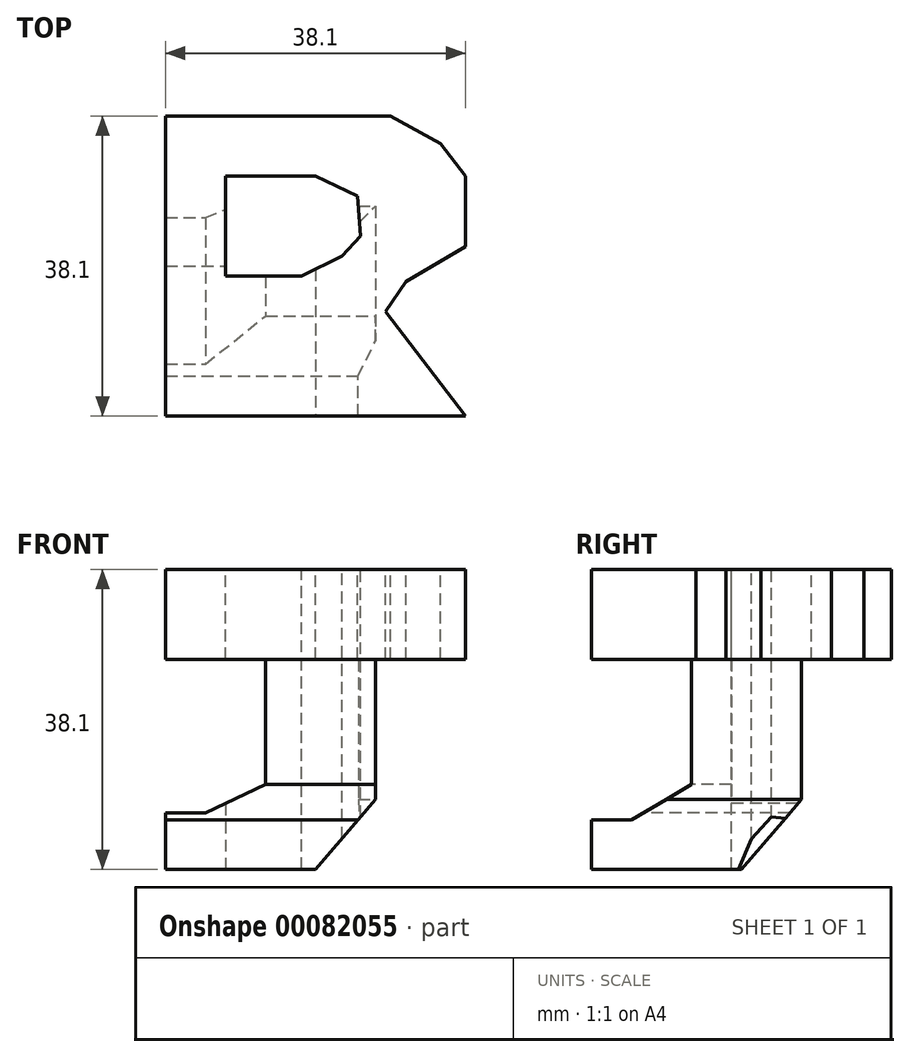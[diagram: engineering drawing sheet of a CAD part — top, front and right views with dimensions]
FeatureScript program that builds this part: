
annotation { "Feature Type Name" : "Feature", "Feature Type Description" : "" }
export const myFeature = defineFeature(function(context is Context, id is Id, definition is map)
    precondition{}
    {
        {
            var Q0;
            Q0=qCreatedBy(makeId("Top.planeOp"),FACE);
            cPlane(context, id + "F0", {"entities" : qUnion([Q0]), "cplaneType" : CPlaneType.OFFSET, "offset" : 38.1 * mm, "width" : 152.4 * mm, "height" : 152.4 * mm});
        }
        {
            var Q0;
            Q0=qCreatedBy(makeId("Front.planeOp"),FACE);
            cPlane(context, id + "F1", {"entities" : qUnion([Q0]), "cplaneType" : CPlaneType.OFFSET, "offset" : 38.1 * mm, "width" : 152.4 * mm, "height" : 152.4 * mm});
        }
        {
            var Q0;
            Q0=qCreatedBy(makeId("Right.planeOp"),FACE);
            cPlane(context, id + "F2", {"entities" : qUnion([Q0]), "cplaneType" : CPlaneType.OFFSET, "offset" : 38.1 * mm, "width" : 152.4 * mm, "height" : 152.4 * mm});
        }
        {
            var Q0;
            Q0=qCreatedBy(makeId("Front.planeOp"),FACE);
            var sketch = newSketch(context, id + "F3", { "sketchPlane" : qUnion([Q0])});
            skLineSegment(sketch, "E0", {"start": v(0, 0) * mm, "end": v(0, 38.1) * mm});
            skLineSegment(sketch, "E1", {"start": v(0, 38.1) * mm, "end": v(38.1, 38.1) * mm});
            skLineSegment(sketch, "E2", {"start": v(38.1, 38.1) * mm, "end": v(38.1, 0) * mm});
            skLineSegment(sketch, "E3", {"start": v(38.1, 0) * mm, "end": v(0, 0) * mm});
            skSolve(sketch);
        }
        {
            var Q0;
            Q0 = qSketchRegion(id + "F3", true);
            extrude(context, id + "F4", {"entities" : qUnion([Q0]), "depth" : 38.1 * mm});
        }
        {
            var Q0;
            Q0=qCreatedBy(id+"F1.planeOp",FACE);
            var sketch = newSketch(context, id + "F5", { "sketchPlane" : qUnion([Q0])});
            skLineSegment(sketch, "E4", {"start": v(0, 0) * mm, "end": v(0, 38.1) * mm});
            skLineSegment(sketch, "E5", {"start": v(0, 38.1) * mm, "end": v(38.1, 38.1) * mm});
            skLineSegment(sketch, "E6", {"start": v(38.1, 38.1) * mm, "end": v(38.1, 0) * mm});
            skLineSegment(sketch, "E7", {"start": v(38.1, 0) * mm, "end": v(0, 0) * mm});
            skLineSegment(sketch, "E8", {"start": v(0, 26.67) * mm, "end": v(12.7, 26.67) * mm});
            skLineSegment(sketch, "E9", {"start": v(38.1, 26.67) * mm, "end": v(26.67, 26.67) * mm});
            skPoint(sketch, "E10.end.orphan", {"position": v(19.05, 0) * mm});
            skLineSegment(sketch, "E11", {"start": v(26.67, 26.67) * mm, "end": v(26.67, 8.89) * mm});
            skLineSegment(sketch, "E12", {"start": v(26.67, 8.89) * mm, "end": v(19.05, 0) * mm});
            skLineSegment(sketch, "E13", {"start": v(12.7, 26.67) * mm, "end": v(12.7, 10.8) * mm});
            skLineSegment(sketch, "E14", {"start": v(12.7, 10.8) * mm, "end": v(5.08, 7.17) * mm});
            skLineSegment(sketch, "E15", {"start": v(5.08, 7.17) * mm, "end": v(0, 7.17) * mm});
            skSolve(sketch);
        }
        {
            var Q0;
            {var subQ0=sQuery(id+"F5.wireOp",EDGE,"E8");Q0=makeQuery(id+"F5.imprint","IMPRINT",FACE,{"disambiguationData":[TD([[makeQuery(id+"F5.imprint","IMPRINT",EDGE,{"derivedFrom":subQ0}),-1.0]])]});}
            var Q1;
            {var subQ0=sQuery(id+"F5.wireOp",EDGE,"E9");Q1=makeQuery(id+"F5.imprint","IMPRINT",FACE,{"disambiguationData":[TD([[makeQuery(id+"F5.imprint","IMPRINT",EDGE,{"derivedFrom":subQ0}),1.0]])]});}
            extrude(context, id + "F6", {"entities" : qUnion([Q0, Q1]), "operationType" : NewBodyOperationType.REMOVE, "oppositeDirection" : true, "depth" : 38.1 * mm});
        }
        {
            var Q0;
            Q0=qCreatedBy(id+"F2.planeOp",FACE);
            var sketch = newSketch(context, id + "F7", { "sketchPlane" : qUnion([Q0])});
            skLineSegment(sketch, "E16", {"start": v(0, 0) * mm, "end": v(0, 38.1) * mm});
            skLineSegment(sketch, "E17", {"start": v(0, 38.1) * mm, "end": v(-38.1, 38.1) * mm});
            skLineSegment(sketch, "E18", {"start": v(-38.1, 38.1) * mm, "end": v(-38.1, 0) * mm});
            skLineSegment(sketch, "E19", {"start": v(-38.1, 0) * mm, "end": v(0, 0) * mm});
            skLineSegment(sketch, "E20", {"start": v(-38.1, 26.67) * mm, "end": v(-25.4, 26.67) * mm});
            skLineSegment(sketch, "E21", {"start": v(-25.4, 26.67) * mm, "end": v(-25.4, 10.8) * mm});
            skLineSegment(sketch, "E22", {"start": v(-25.4, 10.8) * mm, "end": v(-33.02, 6.27) * mm});
            skLineSegment(sketch, "E23", {"start": v(-33.02, 6.27) * mm, "end": v(-38.1, 6.27) * mm});
            skLineSegment(sketch, "E24", {"start": v(0, 26.67) * mm, "end": v(-11.43, 26.67) * mm});
            skLineSegment(sketch, "E25", {"start": v(-11.43, 26.67) * mm, "end": v(-11.43, 8.89) * mm});
            skLineSegment(sketch, "E26", {"start": v(-11.43, 8.89) * mm, "end": v(-19.05, 0) * mm});
            skSolve(sketch);
        }
        {
            var Q0;
            {var subQ0=sQuery(id+"F7.wireOp",EDGE,"E20");Q0=makeQuery(id+"F7.imprint","IMPRINT",FACE,{"disambiguationData":[TD([[makeQuery(id+"F7.imprint","IMPRINT",EDGE,{"derivedFrom":subQ0}),-1.0]])]});}
            var Q1;
            {var subQ0=sQuery(id+"F7.wireOp",EDGE,"E24");Q1=makeQuery(id+"F7.imprint","IMPRINT",FACE,{"disambiguationData":[TD([[makeQuery(id+"F7.imprint","IMPRINT",EDGE,{"derivedFrom":subQ0}),1.0]])]});}
            extrude(context, id + "F8", {"entities" : qUnion([Q0, Q1]), "operationType" : NewBodyOperationType.REMOVE, "oppositeDirection" : true, "depth" : 38.1 * mm});
        }
        {
            var Q0;
            Q0=qCreatedBy(id+"F0.planeOp",FACE);
            var sketch = newSketch(context, id + "F9", { "sketchPlane" : qUnion([Q0])});
            skLineSegment(sketch, "E27", {"start": v(0, 0) * mm, "end": v(38.1, 0) * mm});
            skLineSegment(sketch, "E28", {"start": v(38.1, 0) * mm, "end": v(38.1, -38.1) * mm});
            skLineSegment(sketch, "E29", {"start": v(38.1, -38.1) * mm, "end": v(0, -38.1) * mm});
            skLineSegment(sketch, "E30", {"start": v(0, -38.1) * mm, "end": v(0, 0) * mm});
            skLineSegment(sketch, "E31", {"start": v(7.62, -7.62) * mm, "end": v(19.05, -7.62) * mm});
            skLineSegment(sketch, "E32", {"start": v(19.05, -7.62) * mm, "end": v(24.4, -10.16) * mm});
            skLineSegment(sketch, "E33", {"start": v(24.4, -10.16) * mm, "end": v(24.75, -15.24) * mm});
            skLineSegment(sketch, "E34", {"start": v(24.75, -15.24) * mm, "end": v(22.4, -17.78) * mm});
            skPoint(sketch, "E35.orphan", {"position": v(38.1, -7.62) * mm});
            skPoint(sketch, "E36.end.orphan", {"position": v(0, -21.23) * mm});
            skLineSegment(sketch, "E37", {"start": v(22.4, -17.78) * mm, "end": v(17.3, -20.32) * mm});
            skLineSegment(sketch, "E38", {"start": v(17.3, -20.32) * mm, "end": v(7.62, -20.32) * mm});
            skLineSegment(sketch, "E39", {"start": v(7.62, -7.62) * mm, "end": v(7.62, -20.32) * mm});
            skPoint(sketch, "E40.orphan", {"position": v(0, -7.62) * mm});
            skPoint(sketch, "E41.orphan", {"position": v(0, -20.32) * mm});
            skLineSegment(sketch, "E42", {"start": v(7.62, -29.21) * mm, "end": v(7.62, -38.1) * mm});
            skLineSegment(sketch, "E43", {"start": v(7.62, -38.1) * mm, "end": v(7.62, -29.21) * mm});
            skLineSegment(sketch, "E44", {"start": v(7.62, -29.21) * mm, "end": v(16.51, -29.21) * mm});
            skLineSegment(sketch, "E45", {"start": v(16.51, -29.21) * mm, "end": v(22.86, -38.1) * mm});
            skLineSegment(sketch, "E46", {"start": v(30.53, -21.05) * mm, "end": v(27.94, -24.86) * mm});
            skLineSegment(sketch, "E47", {"start": v(27.94, -24.86) * mm, "end": v(38.1, -38.1) * mm});
            skLineSegment(sketch, "E48", {"start": v(38.1, -7.62) * mm, "end": v(34.95, -3.5) * mm});
            skLineSegment(sketch, "E49", {"start": v(34.95, -3.5) * mm, "end": v(28.56, 0) * mm});
            skPoint(sketch, "E50.start.orphan", {"position": v(38.1, -19.05) * mm});
            skLineSegment(sketch, "E51", {"start": v(30.53, -21.05) * mm, "end": v(38.1, -16.6) * mm});
            skSolve(sketch);
        }
        {
            var Q0;
            {var subQ0=sQuery(id+"F9.wireOp",EDGE,"E43");Q0=makeQuery(id+"F9.imprint","IMPRINT",FACE,{"disambiguationData":[TD([[makeQuery(id+"F9.imprint","IMPRINT",EDGE,{"derivedFrom":subQ0}),-1.0]])]});}
            var Q1;
            Q1=makeQuery(id+"F9.imprint","IMPRINT",FACE,{"disambiguationData":[TD([[makeQuery(id+"F9.imprint","IMPRINT",EDGE,{"derivedFrom":sQuery(id+"F9.wireOp",EDGE,"E31")}),-1.0]])]});
            var Q2;
            Q2=makeQuery(id+"F9.imprint","IMPRINT",FACE,{"disambiguationData":[TD([[makeQuery(id+"F9.imprint","IMPRINT",EDGE,{"derivedFrom":sQuery(id+"F9.wireOp",EDGE,"E46")}),1.0]])]});
            var Q3;
            {var subQ4=sQuery(id+"F9.wireOp",EDGE,"E48");Q3=makeQuery(id+"F9.imprint","IMPRINT",FACE,{"disambiguationData":[TD([[makeQuery(id+"F9.imprint","IMPRINT",EDGE,{"derivedFrom":subQ4}),-1.0]])]});}
            extrude(context, id + "F10", {"entities" : qUnion([Q0, Q1, Q2, Q3]), "operationType" : NewBodyOperationType.REMOVE, "oppositeDirection" : true, "depth" : 38.1 * mm});
        }
    });
